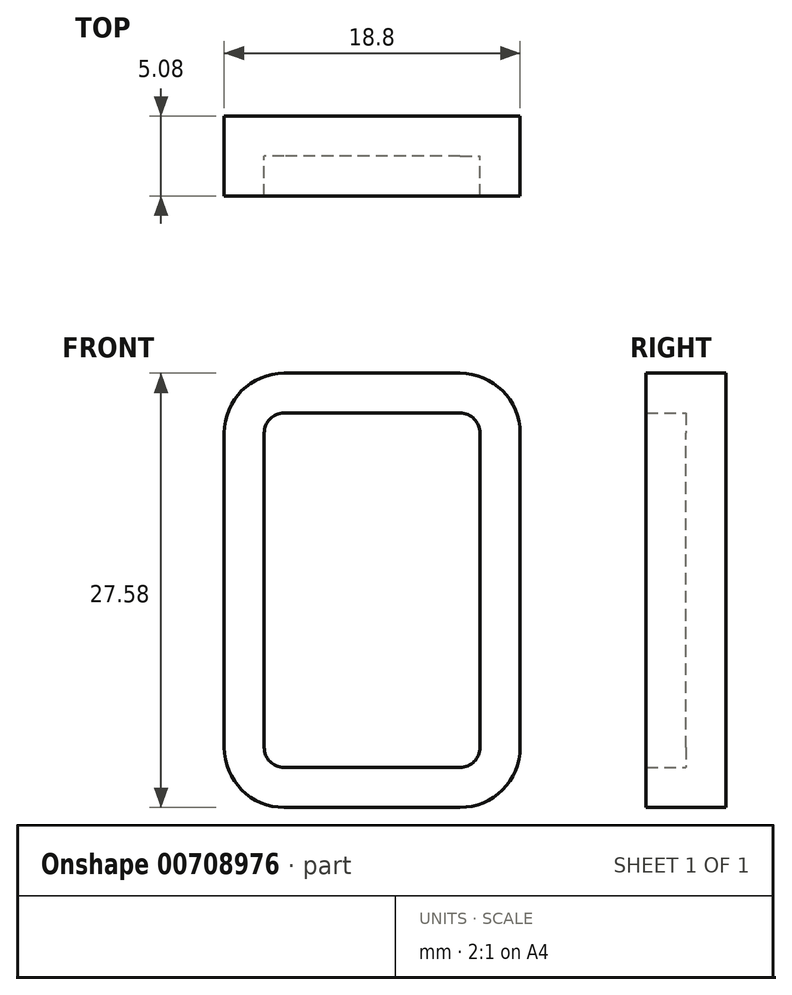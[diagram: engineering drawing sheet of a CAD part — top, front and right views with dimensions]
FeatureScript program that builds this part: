
annotation { "Feature Type Name" : "Feature", "Feature Type Description" : "" }
export const myFeature = defineFeature(function(context is Context, id is Id, definition is map)
    precondition{}
    {
        {
            var Q0;
            Q0=qCreatedBy(makeId("Front.planeOp"),FACE);
            var sketch = newSketch(context, id + "F0", { "sketchPlane" : qUnion([Q0])});
            skLineSegment(sketch, "E0.bottom", {"start": v(5.59, -13.8) * mm, "end": v(-5.59, -13.8) * mm});
            skLineSegment(sketch, "E0.top", {"start": v(5.59, 13.8) * mm, "end": v(-5.59, 13.8) * mm});
            skLineSegment(sketch, "E0.left", {"start": v(9.4, -9.98) * mm, "end": v(9.4, 9.98) * mm});
            skLineSegment(sketch, "E0.right", {"start": v(-9.4, -9.98) * mm, "end": v(-9.4, 9.98) * mm});
            skPoint(sketch, "E0.middle", {"position": v(0, 0) * mm});
            skPoint(sketch, "E1.visualSharp", {"position": v(-9.4, 13.8) * mm});
            skArc(sketch, "E1.filletArc", {"start": v(-5.59, 13.8) * mm, "mid": v(-8.28, 12.68) * mm, "end": v(-9.4, 9.98) * mm});
            skPoint(sketch, "E2.visualSharp", {"position": v(9.4, 13.8) * mm});
            skArc(sketch, "E2.filletArc", {"start": v(9.4, 9.98) * mm, "mid": v(8.28, 12.68) * mm, "end": v(5.59, 13.8) * mm});
            skPoint(sketch, "E3.visualSharp", {"position": v(-9.4, -13.8) * mm});
            skArc(sketch, "E3.filletArc", {"start": v(-9.4, -9.98) * mm, "mid": v(-8.28, -12.68) * mm, "end": v(-5.59, -13.8) * mm});
            skPoint(sketch, "E4.visualSharp", {"position": v(9.4, -13.8) * mm});
            skArc(sketch, "E4.filletArc", {"start": v(5.59, -13.8) * mm, "mid": v(8.28, -12.68) * mm, "end": v(9.4, -9.98) * mm});
            skSolve(sketch);
        }
        {
            var Q0;
            Q0=qSketchRegion(id+"F0",true);
            extrude(context, id + "F1", {"entities" : qUnion([Q0]), "depth" : 5.08 * mm, "offsetDistance" : 25.4 * mm});
        }
        {
            var Q0;
            Q0=makeQuery(id+"F1.opExtrude","CAP_FACE",FACE,{"disambiguationData":[OSD([sQuery(id+"F0.wireOp",EDGE,"E0.bottom"),sQuery(id+"F0.wireOp",EDGE,"E0.top"),sQuery(id+"F0.wireOp",EDGE,"E0.left"),sQuery(id+"F0.wireOp",EDGE,"E0.right"),sQuery(id+"F0.wireOp",EDGE,"E1.filletArc"),sQuery(id+"F0.wireOp",EDGE,"E2.filletArc"),sQuery(id+"F0.wireOp",EDGE,"E3.filletArc"),sQuery(id+"F0.wireOp",EDGE,"E4.filletArc")])],"isStart":false});
            shell(context, id + "F2", {"entities" : qUnion([Q0]), "thickness" : 2.54 * mm});
        }
    });
